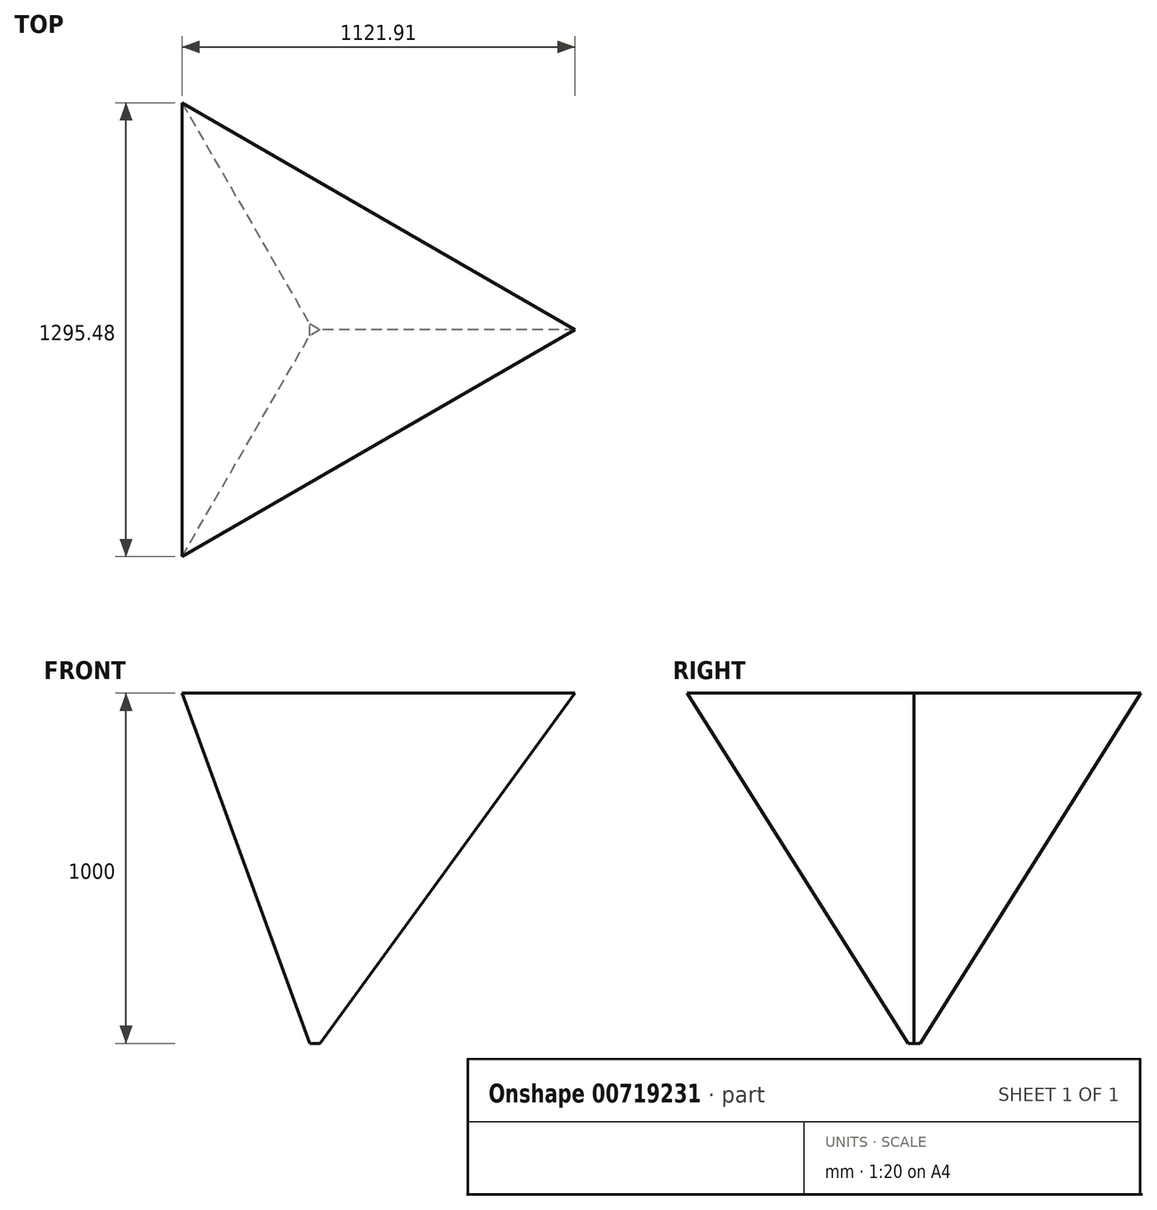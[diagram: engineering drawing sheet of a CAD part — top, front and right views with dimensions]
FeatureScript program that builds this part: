
annotation { "Feature Type Name" : "Feature", "Feature Type Description" : "" }
export const myFeature = defineFeature(function(context is Context, id is Id, definition is map)
    precondition{}
    {
        {
            var Q0;
            Q0=qCreatedBy(makeId("Top.planeOp"),FACE);
            var sketch = newSketch(context, id + "F0", { "sketchPlane" : qUnion([Q0])});
            skCircle(sketch, "E0", {"center": v(0, 0) * mm, "radius": 10 * mm, "construction": true});
            skLineSegment(sketch, "E1", {"start": v(-10, 17.32) * mm, "end": v(-10, -17.32) * mm});
            skLineSegment(sketch, "E2", {"start": v(-10, -17.32) * mm, "end": v(20, 0) * mm});
            skLineSegment(sketch, "E3", {"start": v(20, 0) * mm, "end": v(-10, 17.32) * mm});
            skSolve(sketch);
        }
        {
            var Q0;
            Q0 = qSketchRegion(id + "F0", true);
            extrude(context, id + "F1", {"entities" : qUnion([Q0]), "depth" : 1000 * mm, "offsetDistance" : 25 * mm, "hasDraft" : true, "draftAngle" : 20 * degree});
        }
    });
